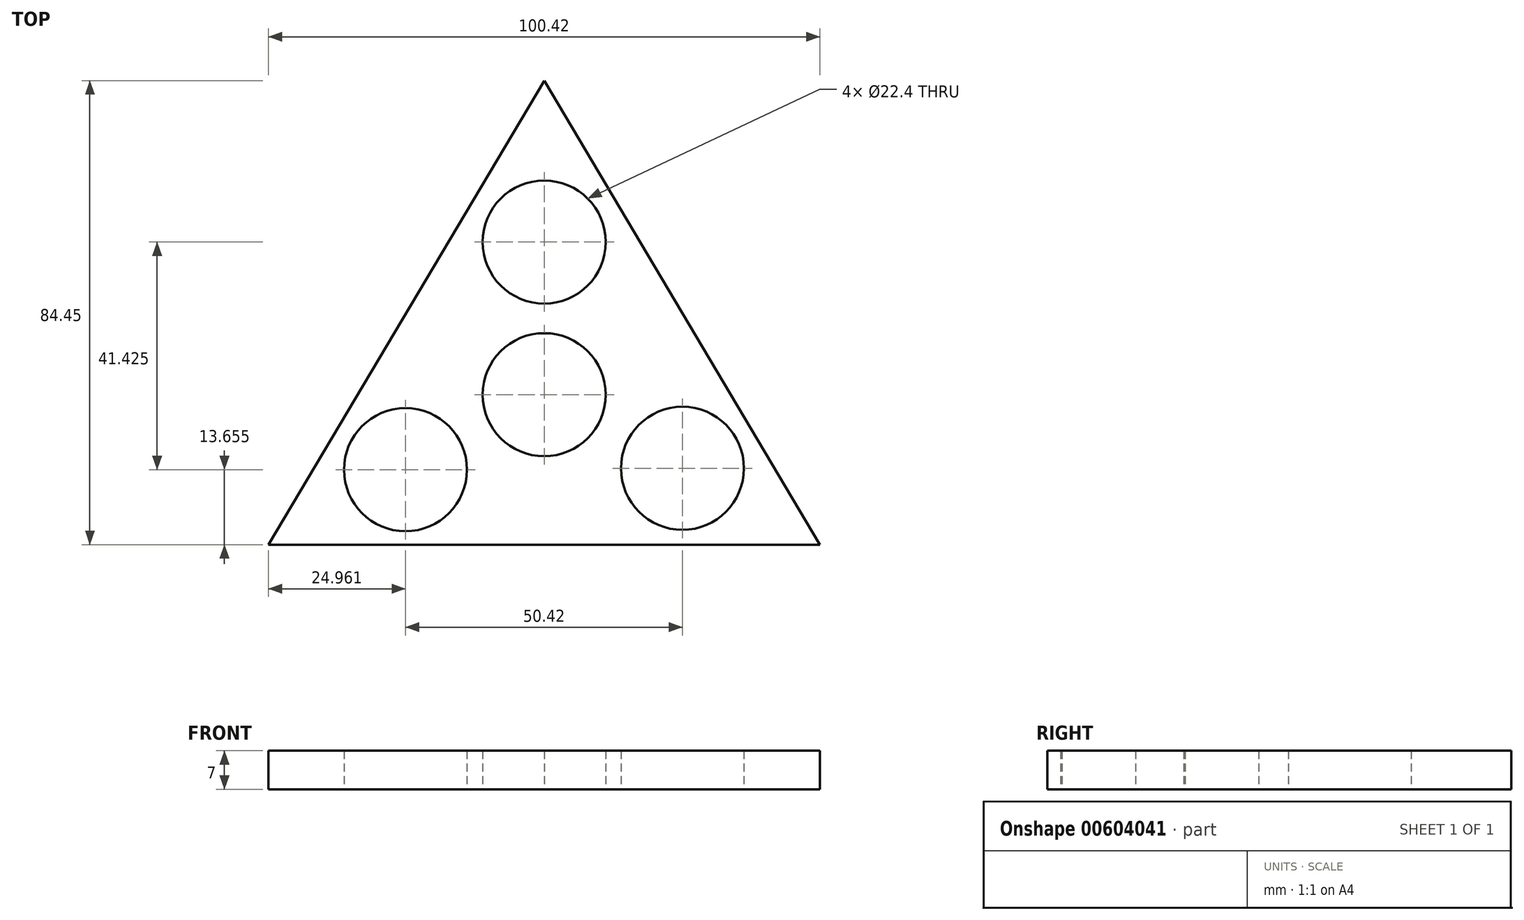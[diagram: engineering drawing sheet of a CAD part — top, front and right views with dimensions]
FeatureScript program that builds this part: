
annotation { "Feature Type Name" : "Feature", "Feature Type Description" : "" }
export const myFeature = defineFeature(function(context is Context, id is Id, definition is map)
    precondition{}
    {
        {
            var Q0;
            Q0=qCreatedBy(makeId("Top.planeOp"),FACE);
            var sketch = newSketch(context, id + "F0", { "sketchPlane" : qUnion([Q0])});
            skCircle(sketch, "E0", {"center": v(0, 0) * mm, "radius": 11.2 * mm});
            skCircle(sketch, "E1", {"center": v(0, 27.78) * mm, "radius": 11.2 * mm});
            skCircle(sketch, "E2", {"center": v(-25.25, -13.64) * mm, "radius": 11.2 * mm});
            skCircle(sketch, "E3", {"center": v(25.17, -13.39) * mm, "radius": 11.2 * mm});
            skPoint(sketch, "E4.start.orphan", {"position": v(0, 47.58) * mm});
            skPoint(sketch, "E5.end.orphan", {"position": v(-13.73, 8.48) * mm});
            skPoint(sketch, "E5.start.orphan", {"position": v(-21.93, 20.55) * mm});
            skPoint(sketch, "E6.start.orphan", {"position": v(-30.14, 0) * mm});
            skPoint(sketch, "E7.start.orphan", {"position": v(-44.46, -24.82) * mm});
            skPoint(sketch, "E8.start.orphan", {"position": v(-13.73, -26.91) * mm});
            skPoint(sketch, "E9.start.orphan", {"position": v(0, -13.07) * mm});
            skPoint(sketch, "E10.start.orphan", {"position": v(13.94, -26.91) * mm});
            skPoint(sketch, "E11.start.orphan", {"position": v(43.55, -24.82) * mm});
            skPoint(sketch, "E12.start.orphan", {"position": v(31.32, 0) * mm});
            skPoint(sketch, "E13.end.orphan", {"position": v(26.5, 20.55) * mm});
            skPoint(sketch, "E13.start.orphan", {"position": v(16.68, 8.48) * mm});
            skCircle(sketch, "E14", {"center": v(0, 0) * mm, "radius": 57.15 * mm});
            skLineSegment(sketch, "E15", {"start": v(0, 57.15) * mm, "end": v(50.2, -27.3) * mm});
            skLineSegment(sketch, "E16", {"start": v(50.2, -27.3) * mm, "end": v(-50.2, -27.3) * mm});
            skLineSegment(sketch, "E17", {"start": v(-50.2, -27.3) * mm, "end": v(0, 57.15) * mm});
            skSolve(sketch);
        }
        {
            var Q0;
            Q0=makeQuery(id+"F0.imprint","IMPRINT",FACE,{"disambiguationData":[TD([[makeQuery(id+"F0.imprint","IMPRINT",EDGE,{"derivedFrom":sQuery(id+"F0.wireOp",EDGE,"E0")}),-1.0]])]});
            extrude(context, id + "F1", {"entities" : qUnion([Q0]), "depth" : 7 * mm, "offsetDistance" : 25 * mm});
        }
    });
